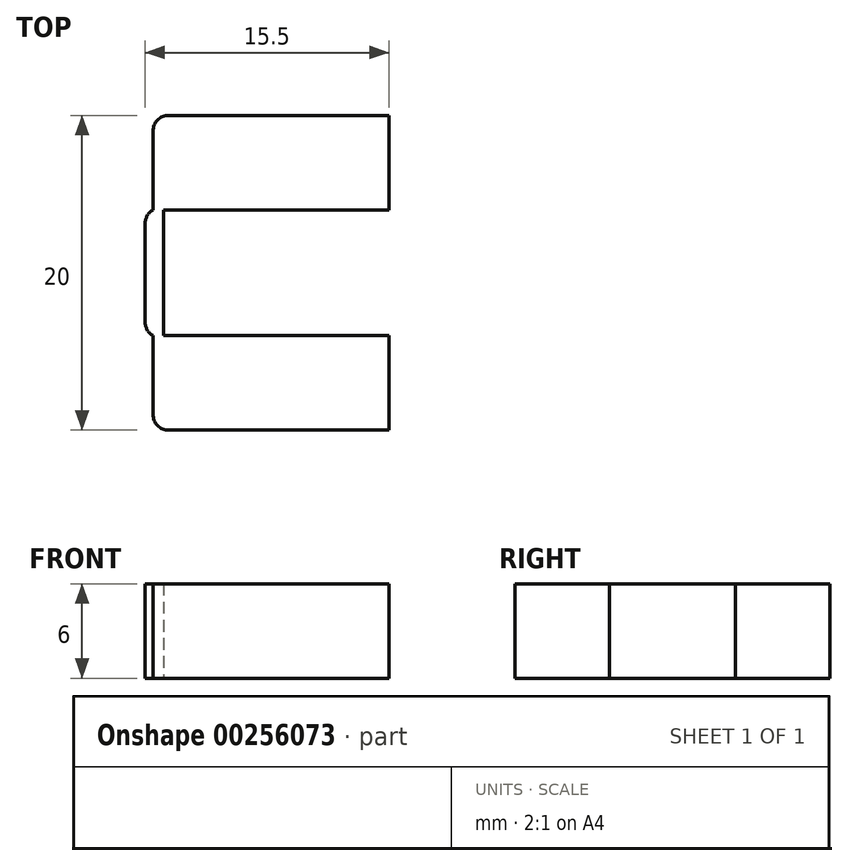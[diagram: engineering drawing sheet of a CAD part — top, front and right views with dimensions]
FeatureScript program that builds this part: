
annotation { "Feature Type Name" : "Feature", "Feature Type Description" : "" }
export const myFeature = defineFeature(function(context is Context, id is Id, definition is map)
    precondition{}
    {
        {
            var Q0;
            Q0=qCreatedBy(makeId("Top.planeOp"),FACE);
            var sketch = newSketch(context, id + "F0", { "sketchPlane" : qUnion([Q0])});
            skLineSegment(sketch, "E0", {"start": v(0, 0) * mm, "end": v(15, 0) * mm});
            skLineSegment(sketch, "E1", {"start": v(15, 0) * mm, "end": v(15, -6) * mm});
            skLineSegment(sketch, "E2", {"start": v(15, -6) * mm, "end": v(0, -6) * mm});
            skLineSegment(sketch, "E3", {"start": v(0, -4) * mm, "end": v(0, 0) * mm});
            skLineSegment(sketch, "E4", {"start": v(0, -6) * mm, "end": v(-0.5, -6) * mm});
            skLineSegment(sketch, "E5", {"start": v(-0.5, -6) * mm, "end": v(-0.5, -14) * mm});
            skLineSegment(sketch, "E6", {"start": v(-0.5, -14) * mm, "end": v(0, -14) * mm});
            skLineSegment(sketch, "E7", {"start": v(0, -14) * mm, "end": v(15, -14) * mm});
            skLineSegment(sketch, "E8", {"start": v(15, -14) * mm, "end": v(15, -20) * mm});
            skLineSegment(sketch, "E9", {"start": v(15, -20) * mm, "end": v(0, -20) * mm});
            skLineSegment(sketch, "E10", {"start": v(0, -20) * mm, "end": v(0, -16) * mm});
            skLineSegment(sketch, "E11", {"start": v(0.67, -14) * mm, "end": v(0.67, -6) * mm});
            skLineSegment(sketch, "E12", {"start": v(0.67, -6) * mm, "end": v(0, -6) * mm});
            skLineSegment(sketch, "E13", {"start": v(0, -14) * mm, "end": v(0.67, -14) * mm});
            skLineSegment(sketch, "E14", {"start": v(0, -6) * mm, "end": v(0, -4) * mm});
            skLineSegment(sketch, "E15", {"start": v(0, -14) * mm, "end": v(0, -16) * mm});
            skSolve(sketch);
        }
        {
            var Q0;
            Q0=makeQuery(id+"F0.imprint","IMPRINT",FACE,{"disambiguationData":[TD([[makeQuery(id+"F0.imprint","IMPRINT",EDGE,{"derivedFrom":sQuery(id+"F0.wireOp",EDGE,"E0")}),-1.0]])]});
            var Q1;
            {var subQ1=sQuery(id+"F0.wireOp",EDGE,"E5");Q1=makeQuery(id+"F0.imprint","IMPRINT",FACE,{"disambiguationData":[TD([[makeQuery(id+"F0.imprint","IMPRINT",EDGE,{"derivedFrom":subQ1}),1.0]])]});}
            var Q2;
            Q2=makeQuery(id+"F0.imprint","IMPRINT",FACE,{"disambiguationData":[TD([[makeQuery(id+"F0.imprint","IMPRINT",EDGE,{"derivedFrom":sQuery(id+"F0.wireOp",EDGE,"E7")}),-1.0]])]});
            extrude(context, id + "F1", {"entities" : qUnion([Q0, Q1, Q2]), "depth" : 6 * mm});
        }
        {
            var Q0;
            Q0=makeQuery(id+"F1.opExtrude","SWEPT_EDGE",EDGE,{"disambiguationData":[OSD([sQuery(id+"F0.wireOp",EDGE,"E4"),sQuery(id+"F0.wireOp",EDGE,"E5")])]});
            var Q1;
            Q1=makeQuery(id+"F1.opExtrude","SWEPT_EDGE",EDGE,{"disambiguationData":[OSD([sQuery(id+"F0.wireOp",EDGE,"E5"),sQuery(id+"F0.wireOp",EDGE,"E6")])]});
            var Q2;
            Q2=makeQuery(id+"F1.opExtrude","SWEPT_EDGE",EDGE,{"disambiguationData":[OSD([sQuery(id+"F0.wireOp",EDGE,"E0"),sQuery(id+"F0.wireOp",EDGE,"E3")])]});
            var Q3;
            Q3=makeQuery(id+"F1.opExtrude","SWEPT_EDGE",EDGE,{"disambiguationData":[OSD([sQuery(id+"F0.wireOp",EDGE,"E9"),sQuery(id+"F0.wireOp",EDGE,"E10")])]});
            fillet(context, id + "F2", {"entities" : qUnion([Q0, Q1, Q2, Q3]), "radius" : 1 * mm, "tangentPropagation" : true, "allowEdgeOverflow" : false});
        }
    });
